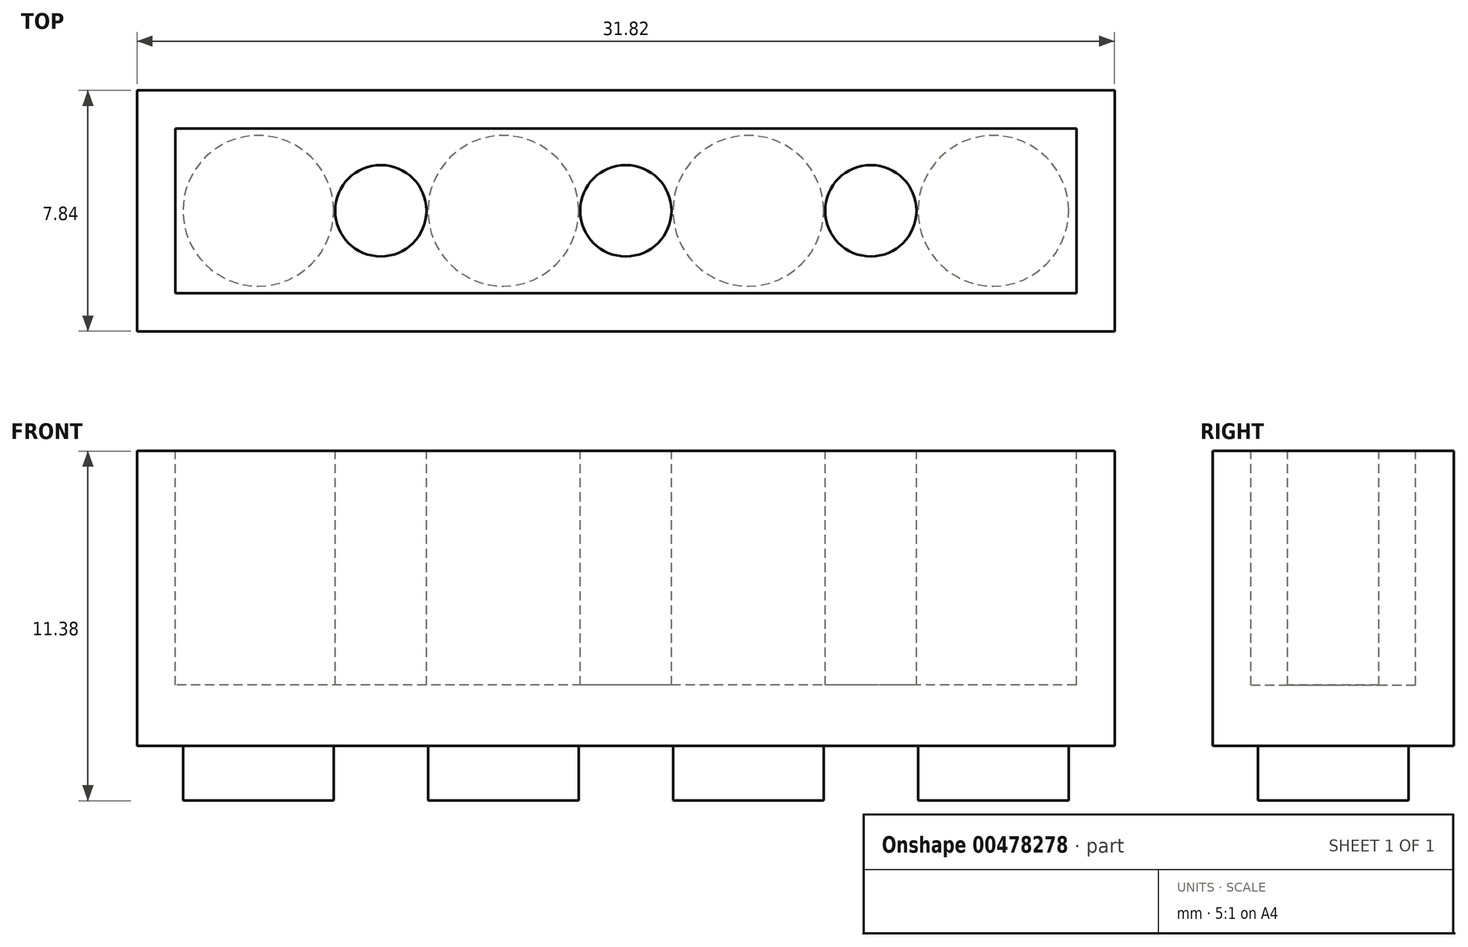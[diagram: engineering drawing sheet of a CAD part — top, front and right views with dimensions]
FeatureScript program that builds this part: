
annotation { "Feature Type Name" : "Feature", "Feature Type Description" : "" }
export const myFeature = defineFeature(function(context is Context, id is Id, definition is map)
    precondition{}
    {
        {
            var Q0;
            Q0=qCreatedBy(makeId("Top.planeOp"),FACE);
            var sketch = newSketch(context, id + "F0", { "sketchPlane" : qUnion([Q0])});
            skLineSegment(sketch, "E0.bottom", {"start": v(-15.91, 3.92) * mm, "end": v(15.91, 3.92) * mm});
            skLineSegment(sketch, "E0.top", {"start": v(-15.91, -3.92) * mm, "end": v(15.91, -3.92) * mm});
            skLineSegment(sketch, "E0.left", {"start": v(-15.91, 3.92) * mm, "end": v(-15.91, -3.92) * mm});
            skLineSegment(sketch, "E0.right", {"start": v(15.91, 3.92) * mm, "end": v(15.91, -3.92) * mm});
            skPoint(sketch, "E0.middle", {"position": v(0, 0) * mm});
            skSolve(sketch);
        }
        {
            var Q0;
            Q0=makeQuery(id+"F0.imprint","IMPRINT",FACE,{"disambiguationData":[TD([[makeQuery(id+"F0.imprint","IMPRINT",EDGE,{"derivedFrom":sQuery(id+"F0.wireOp",EDGE,"E0.bottom")}),-1.0]])]});
            var sketch = newSketch(context, id + "F1", { "sketchPlane" : qUnion([Q0])});
            skCircle(sketch, "E1", {"center": v(-11.96, 0) * mm, "radius": 2.45 * mm});
            skCircle(sketch, "E2", {"center": v(-3.99, 0) * mm, "radius": 2.45 * mm});
            skCircle(sketch, "E3", {"center": v(3.99, 0) * mm, "radius": 2.45 * mm});
            skCircle(sketch, "E4", {"center": v(11.96, 0) * mm, "radius": 2.45 * mm});
            skSolve(sketch);
        }
        {
            var Q0;
            Q0 = qSketchRegion(id + "F0", true);
            extrude(context, id + "F2", {"entities" : qUnion([Q0]), "depth" : 9.6 * mm, "offsetDistance" : 25.4 * mm});
        }
        {
            var Q0;
            Q0=makeQuery(id+"F1.imprint","IMPRINT",FACE,{"disambiguationData":[TD([[makeQuery(id+"F1.imprint","IMPRINT",EDGE,{"derivedFrom":sQuery(id+"F1.wireOp",EDGE,"E1")}),1.0]])]});
            var Q1;
            Q1=makeQuery(id+"F1.imprint","IMPRINT",FACE,{"disambiguationData":[TD([[makeQuery(id+"F1.imprint","IMPRINT",EDGE,{"derivedFrom":sQuery(id+"F1.wireOp",EDGE,"E2")}),1.0]])]});
            var Q2;
            Q2=makeQuery(id+"F1.imprint","IMPRINT",FACE,{"disambiguationData":[TD([[makeQuery(id+"F1.imprint","IMPRINT",EDGE,{"derivedFrom":sQuery(id+"F1.wireOp",EDGE,"E3")}),1.0]])]});
            var Q3;
            Q3=makeQuery(id+"F1.imprint","IMPRINT",FACE,{"disambiguationData":[TD([[makeQuery(id+"F1.imprint","IMPRINT",EDGE,{"derivedFrom":sQuery(id+"F1.wireOp",EDGE,"E4")}),1.0]])]});
            extrude(context, id + "F3", {"entities" : qUnion([Q0, Q1, Q2, Q3]), "operationType" : NewBodyOperationType.ADD, "oppositeDirection" : true, "depth" : 1.78 * mm, "offsetDistance" : 25.4 * mm});
        }
        {
            var Q0;
            Q0=makeQuery(id+"F2.opExtrude","CAP_FACE",FACE,{"disambiguationData":[OSD([sQuery(id+"F0.wireOp",EDGE,"E0.bottom"),sQuery(id+"F0.wireOp",EDGE,"E0.top"),sQuery(id+"F0.wireOp",EDGE,"E0.left"),sQuery(id+"F0.wireOp",EDGE,"E0.right")])],"isStart":false});
            var sketch = newSketch(context, id + "F4", { "sketchPlane" : qUnion([Q0])});
            skLineSegment(sketch, "E5.bottom", {"start": v(14.67, -2.68) * mm, "end": v(-14.67, -2.68) * mm});
            skLineSegment(sketch, "E5.top", {"start": v(14.67, 2.68) * mm, "end": v(-14.67, 2.68) * mm});
            skLineSegment(sketch, "E5.left", {"start": v(14.67, -2.68) * mm, "end": v(14.67, 2.68) * mm});
            skLineSegment(sketch, "E5.right", {"start": v(-14.67, -2.68) * mm, "end": v(-14.67, 2.68) * mm});
            skPoint(sketch, "E5.middle", {"position": v(0, 0) * mm});
            skSolve(sketch);
        }
        {
            var Q0;
            Q0=makeQuery(id+"F4.imprint","IMPRINT",FACE,{"disambiguationData":[TD([[makeQuery(id+"F4.imprint","IMPRINT",EDGE,{"derivedFrom":sQuery(id+"F4.wireOp",EDGE,"E5.bottom")}),-1.0]])]});
            var sketch = newSketch(context, id + "F5", { "sketchPlane" : qUnion([Q0])});
            skCircle(sketch, "E6", {"center": v(-7.98, 0) * mm, "radius": 1.49 * mm});
            skCircle(sketch, "E7", {"center": v(0, 0) * mm, "radius": 1.49 * mm});
            skCircle(sketch, "E8", {"center": v(7.98, 0) * mm, "radius": 1.49 * mm});
            skSolve(sketch);
        }
        {
            var Q0;
            Q0=makeQuery(id+"F4.imprint","IMPRINT",FACE,{"disambiguationData":[TD([[makeQuery(id+"F4.imprint","IMPRINT",EDGE,{"derivedFrom":sQuery(id+"F4.wireOp",EDGE,"E5.bottom")}),-1.0]])]});
            extrude(context, id + "F6", {"entities" : qUnion([Q0]), "operationType" : NewBodyOperationType.REMOVE, "oppositeDirection" : true, "depth" : 7.62 * mm, "offsetDistance" : 25.4 * mm});
        }
        {
            var Q0;
            Q0=makeQuery(id+"F5.imprint","IMPRINT",FACE,{"disambiguationData":[TD([[makeQuery(id+"F5.imprint","IMPRINT",EDGE,{"derivedFrom":sQuery(id+"F5.wireOp",EDGE,"E6")}),1.0]])]});
            var Q1;
            Q1=makeQuery(id+"F5.imprint","IMPRINT",FACE,{"disambiguationData":[TD([[makeQuery(id+"F5.imprint","IMPRINT",EDGE,{"derivedFrom":sQuery(id+"F5.wireOp",EDGE,"E7")}),1.0]])]});
            var Q2;
            Q2=makeQuery(id+"F5.imprint","IMPRINT",FACE,{"disambiguationData":[TD([[makeQuery(id+"F5.imprint","IMPRINT",EDGE,{"derivedFrom":sQuery(id+"F5.wireOp",EDGE,"E8")}),1.0]])]});
            extrude(context, id + "F7", {"entities" : qUnion([Q0, Q1, Q2]), "operationType" : NewBodyOperationType.ADD, "oppositeDirection" : true, "depth" : 8.13 * mm, "offsetDistance" : 25.4 * mm});
        }
    });
